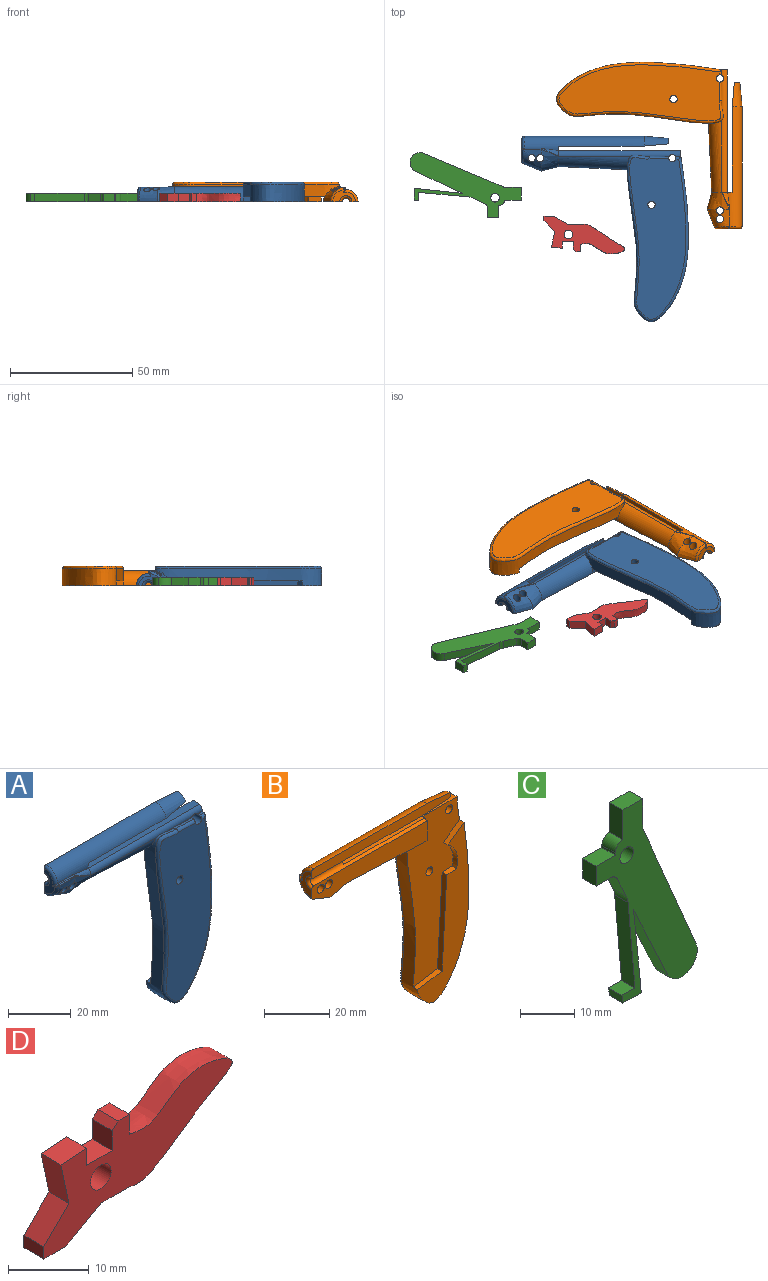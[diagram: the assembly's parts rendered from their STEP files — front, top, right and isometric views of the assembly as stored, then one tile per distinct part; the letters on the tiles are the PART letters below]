
ASSEMBLY  parts=4 mates=2
PART A: 55 faces, bbox 68.7x11.1x76.8 mm
  f0: plane 6.97x5.07mm, normal (-0.59,0,0.81), area 17.2mm2, adj f1,f22,f32,f54
  f1: extruded ~68.03x24.91mm, area 868.2mm2, adj f0,f6,f7,f8,f9,f10,f11,f22
  f2: cylinder r=1.5mm len=6mm, axis (0,1,0), area 56.5mm2, adj f22,f25
  f3: cylinder r=1.5mm len=6mm, axis (0,-1,0), area 49.7mm2, adj f5,f7,f8,f22,f23,f24,f25,f26
  f4: plane 7.88x2mm, normal (1,0,0), area 15.4mm2, adj f12,f13,f22,f30,f52
  f5: extruded ~7.96x0.14mm, area 0.5mm2, adj f3,f8,f23
  f6: extruded ~2.28x0.17mm, area 0.3mm2, adj f1,f8,f9
  f7: extruded ~2.24x0.24mm, area 0.4mm2, adj f1,f3,f8,f11,f24
  f8: cylinder r=2mm len=50mm, axis (1,0,0), area 131.6mm2, adj f1,f3,f5,f6,f7,f9,f10,f11
  f9: bspline ~35x2.96mm, area 0mm2, adj f1,f6,f8
  f10: bspline ~35x9.07mm, area 238.8mm2, adj f1,f8,f36,f49,f52
  f11: plane 4.12x2.43mm, normal (1,0,0), area 9.4mm2, adj f1,f7,f8,f13,f22
  f12: cylinder r=1.5mm len=49mm, axis (-1,0,0), area 154.3mm2, adj f4,f13,f16,f17,f20,f43,f52,f53
  f13: plane 50x3.78mm, normal (0,0,1), area 175.8mm2, adj f4,f8,f11,f12,f16,f22
  f14: cylinder r=5mm len=49mm, axis (-1,0,0), area 353.1mm2, adj f16,f17,f18,f35,f38,f41,f42,f53
  f15: plane 9.32x4.92mm, normal (-1,0,0), area 22.6mm2, adj f39,f40,f41,f43,f52,f53
  f16: plane 3.88x2mm, normal (1,0,0), area 7.2mm2, adj f12,f13,f14,f17
  f17: plane 35x3.78mm, normal (0,0,-1), area 132.3mm2, adj f12,f14,f16,f19
  f18: cone r=5mm half-angle=5deg, axis (-1,0,0), area 56.7mm2, adj f14,f19,f21,f53
  f19: plane 10.15x3.93mm, normal (0.09,0,-1), area 30.3mm2, adj f17,f18,f20,f21
  f20: cone r=1.5mm half-angle=5deg, axis (1,0,0), area 14.5mm2, adj f12,f19,f21,f53
  f21: plane 3.67x2.25mm, normal (1,0,0), area 5.4mm2, adj f18,f19,f20,f53
  f22: plane 62.43x23.55mm, normal (0,1,0), area 825.1mm2, adj f0,f1,f2,f3,f4,f11,f13,f29
  f23: plane 7.88x0.92mm, normal (0.02,0,1), area 7.2mm2, adj f1,f3,f5,f26
  f24: plane 2.14x0.93mm, normal (0.02,0,1), area 2mm2, adj f1,f3,f7,f28
  f25: plane 66.12x23.01mm, normal (0,-1,0), area 1183.2mm2, adj f2,f3,f26,f27,f28
  f26: cylinder r=1mm len=7.9mm, axis (1,0,-0.02), area 12.2mm2, adj f3,f23,f25,f27
  f27: bspline ~68.87x25.01mm, area 235.8mm2, adj f1,f25,f26,f28
  f28: cylinder r=1mm len=2.15mm, axis (1,0,-0.02), area 2.6mm2, adj f3,f24,f25,f27
  f29: plane 3.9x2mm, normal (-0.05,0,-1), area 7.8mm2, adj f1,f22,f30,f52
  f30: plane 3x2mm, normal (0,0,-1), area 6mm2, adj f4,f22,f29,f52
  f31: plane 4.22x2mm, normal (-0.01,0,1), area 8.4mm2, adj f22,f32,f34,f54
  f32: cylinder r=9.32mm len=10.8mm, axis (0,-1,0), area 24.5mm2, adj f0,f22,f31,f54
  f33: plane 10.54x2mm, normal (-0.16,0,0.99), area 21.4mm2, adj f1,f22,f34,f54
  f34: plane 35.08x2.01mm, normal (-1,0,0.06), area 70.3mm2, adj f22,f31,f33,f54
  f35: bspline ~6.93x3.14mm, area 10.4mm2, adj f8,f14,f42,f49
  f36: bspline ~9.22x7.64mm, area 67mm2, adj f10,f37,f48,f49,f50,f52
  f37: bspline ~9.22x8mm, area 64.2mm2, adj f36,f40,f45,f46,f47,f50,f51,f52
  f38: plane 6.93x0.7mm, normal (0,0,1), area 4.8mm2, adj f14,f39,f42,f46
  f39: cylinder r=1mm len=1.82mm, axis (0,1,0), area 1.3mm2, adj f15,f38,f41,f44,f45
  f40: bspline ~6.69x6.19mm, area 11.5mm2, adj f15,f37,f44,f52
  f41: torus R=4mm, axis (1,0,0), area 12.3mm2, adj f14,f15,f39,f53
  f42: bspline ~0.95x0.37mm, area 0.2mm2, adj f14,f35,f38,f47,f48
  f43: torus R=2.5mm, axis (1,0,0), area 9.2mm2, adj f12,f15,f52,f53
  f44: bspline ~1.18x1.1mm, area 0.4mm2, adj f39,f40,f45
  f45: bspline ~0.38x0.33mm, area 0mm2, adj f37,f39,f44,f46
  f46: bspline ~9.22x0.32mm, area 3.3mm2, adj f37,f38,f45,f47
  f47: bspline ~0.69x0.38mm, area 0.1mm2, adj f37,f42,f46,f48
  f48: bspline ~0.45x0.39mm, area 0mm2, adj f36,f42,f47,f49
  f49: bspline ~9.42x4.26mm, area 1.3mm2, adj f8,f10,f35,f36,f48
  f50: cylinder r=1.5mm len=5.76mm, axis (0,-1,0), area 49.5mm2, adj f36,f37,f52
  f51: cylinder r=1.5mm len=5.66mm, axis (0,-1,0), area 46.8mm2, adj f37,f52
  f52: plane 50.02x7.74mm, normal (0,1,0), area 316.7mm2, adj f4,f10,f12,f15,f29,f30,f36,f37
  f53: plane 60x3.5mm, normal (0,1,0), area 200.8mm2, adj f12,f14,f15,f18,f20,f21,f41,f43
  f54: plane 61.62x23.07mm, normal (0,1,0), area 509.6mm2, adj f0,f1,f31,f32,f33,f34
PART B: 55 faces, bbox 68.7x11.1x76.8 mm
  f0: plane 6.97x5.07mm, normal (-0.59,0,0.81), area 17.2mm2, adj f1,f13,f34,f54
  f1: extruded ~68.03x24.91mm, area 868.2mm2, adj f0,f3,f10,f14,f24,f25,f28,f29
  f2: plane 7.88x2mm, normal (1,0,0), area 15.4mm2, adj f4,f11,f27,f34,f52
  f3: bspline ~35x9.07mm, area 238.8mm2, adj f1,f16,f32,f51,f52
  f4: cylinder r=1.5mm len=49mm, axis (-1,0,0), area 154.3mm2, adj f2,f8,f20,f27,f30,f31,f52,f53
  f5: cylinder r=5mm len=49mm, axis (-1,0,0), area 353.1mm2, adj f7,f19,f30,f31,f42,f43,f45,f53
  f6: plane 9.32x4.92mm, normal (-1,0,0), area 22.6mm2, adj f18,f19,f20,f44,f52,f53
  f7: cone r=5mm half-angle=5deg, axis (-1,0,0), area 56.7mm2, adj f5,f9,f33,f53
  f8: cone r=1.5mm half-angle=5deg, axis (1,0,0), area 14.5mm2, adj f4,f9,f33,f53
  f9: plane 3.67x2.25mm, normal (1,0,0), area 5.4mm2, adj f7,f8,f33,f53
  f10: plane 3.9x2mm, normal (-0.05,0,-1), area 7.8mm2, adj f1,f11,f34,f52
  f11: plane 3x2mm, normal (0,0,-1), area 6mm2, adj f2,f10,f34,f52
  f12: plane 4.22x2mm, normal (-0.01,0,1), area 8.4mm2, adj f13,f15,f34,f54
  f13: cylinder r=9.32mm len=10.8mm, axis (0,-1,0), area 24.5mm2, adj f0,f12,f34,f54
  f14: plane 10.54x2mm, normal (-0.16,0,0.99), area 21.4mm2, adj f1,f15,f34,f54
  f15: plane 35.08x2.01mm, normal (-1,0,0.06), area 70.3mm2, adj f12,f14,f34,f54
  f16: bspline ~9.22x7.64mm, area 67mm2, adj f3,f17,f21,f50,f51,f52
  f17: bspline ~8.98x7.37mm, area 64.2mm2, adj f16,f18,f21,f22,f47,f48,f49,f52
  f18: bspline ~6.73x6.23mm, area 11.5mm2, adj f6,f17,f46,f52
  f19: torus R=4mm, axis (1,0,0), area 12.3mm2, adj f5,f6,f44,f53
  f20: torus R=2.5mm, axis (1,0,0), area 9.2mm2, adj f4,f6,f52,f53
  f21: cylinder r=1.5mm len=5.76mm, axis (0,-1,0), area 49.5mm2, adj f16,f17,f52
  f22: cylinder r=1.5mm len=5.66mm, axis (0,-1,0), area 46.8mm2, adj f17,f52
  f23: cylinder r=1.5mm len=6mm, axis (0,-1,0), area 49.7mm2, adj f25,f26,f32,f34,f35,f36,f37,f39
  f24: bspline ~35x2.96mm, area 0mm2, adj f1,f28,f32
  f25: extruded ~2.24x0.24mm, area 0.4mm2, adj f1,f23,f29,f32,f36
  f26: extruded ~7.96x0.14mm, area 0.5mm2, adj f23,f32,f35
  f27: plane 50x3.78mm, normal (0,0,1), area 175.8mm2, adj f2,f4,f29,f30,f32,f34
  f28: extruded ~2.28x0.17mm, area 0.3mm2, adj f1,f24,f32
  f29: plane 4.12x2.43mm, normal (1,0,0), area 9.4mm2, adj f1,f25,f27,f32,f34
  f30: plane 3.88x2mm, normal (1,0,0), area 7.2mm2, adj f4,f5,f27,f31
  f31: plane 35x3.78mm, normal (0,0,-1), area 132.3mm2, adj f4,f5,f30,f33
  f32: cylinder r=2mm len=50mm, axis (-1,0,0), area 131.6mm2, adj f1,f3,f23,f24,f25,f26,f27,f28
  f33: plane 10.15x3.93mm, normal (0.09,0,-1), area 30.3mm2, adj f7,f8,f9,f31
  f34: plane 62.43x23.55mm, normal (0,-1,0), area 825.1mm2, adj f0,f1,f2,f10,f11,f12,f13,f14
  f35: plane 7.88x0.92mm, normal (0.02,0,1), area 7.2mm2, adj f1,f23,f26,f39
  f36: plane 2.14x0.93mm, normal (0.02,0,1), area 2mm2, adj f1,f23,f25,f41
  f37: plane 66.12x23.01mm, normal (0,1,0), area 1183.1mm2, adj f23,f38,f39,f40,f41
  f38: cylinder r=1.5mm len=6mm, axis (0,1,0), area 56.5mm2, adj f34,f37
  f39: cylinder r=1mm len=7.9mm, axis (-1,0,0.02), area 12.2mm2, adj f23,f35,f37,f40
  f40: bspline ~68.88x25.01mm, area 235.9mm2, adj f1,f37,f39,f41
  f41: cylinder r=1mm len=2.15mm, axis (-1,0,0.02), area 2.6mm2, adj f23,f36,f37,f40
  f42: bspline ~6.93x3.14mm, area 10.4mm2, adj f5,f32,f45,f51
  f43: plane 6.93x0.7mm, normal (0,0,1), area 4.8mm2, adj f5,f44,f45,f48
  f44: cylinder r=1mm len=1.82mm, axis (0,1,0), area 1.3mm2, adj f6,f19,f43,f46,f47
  f45: bspline ~0.95x0.37mm, area 0.2mm2, adj f5,f42,f43,f49,f50
  f46: bspline ~1.18x1.1mm, area 0.4mm2, adj f18,f44,f47
  f47: bspline ~0.38x0.33mm, area 0mm2, adj f17,f44,f46,f48
  f48: bspline ~9.22x0.32mm, area 3.3mm2, adj f17,f43,f47,f49
  f49: bspline ~0.68x0.38mm, area 0.1mm2, adj f17,f45,f48,f50
  f50: bspline ~0.45x0.38mm, area 0mm2, adj f16,f45,f49,f51
  f51: bspline ~9.67x4.37mm, area 1.3mm2, adj f3,f16,f32,f42,f50
  f52: plane 50.02x7.74mm, normal (0,-1,0), area 316.7mm2, adj f2,f3,f4,f6,f10,f11,f16,f17
  f53: plane 60x3.5mm, normal (0,-1,0), area 200.8mm2, adj f4,f5,f6,f7,f8,f9,f19,f20
  f54: plane 61.62x23.07mm, normal (0,-1,0), area 509.6mm2, adj f0,f1,f12,f13,f14,f15
PART C: 26 faces, bbox 26.5x3.5x45.5 mm
  f0: plane 19.21x8.96mm, normal (-0.91,0,-0.42), area 74.2mm2, adj f9,f10,f16,f20
  f1: plane 3.5x0.5mm, normal (-1,0,0), area 1.8mm2, adj f9,f10,f11,f14
  f2: plane 5.1x3.5mm, normal (-0.91,0,-0.42), area 19.7mm2, adj f9,f10,f15,f25
  f3: plane 3.5x0.13mm, normal (0.39,0,-0.92), area 0.5mm2, adj f9,f10,f16,f17
  f4: plane 32.43x13.67mm, normal (0.92,0,0.39), area 123.2mm2, adj f9,f10,f17,f18
  f5: plane 5.89x3.5mm, normal (1,0,0), area 20.6mm2, adj f6,f9,f10,f18
  f6: plane 5.2x3.5mm, normal (0,0,1), area 18.2mm2, adj f5,f7,f9,f10
  f7: plane 6.7x3.5mm, normal (-1,0,0), area 23.4mm2, adj f6,f9,f10,f14
  f8: cylinder r=1.75mm len=3.5mm, axis (0,1,0), area 38.5mm2, adj f9,f10
  f9: plane 45.48x26.5mm, normal (0,-1,0), area 433.5mm2, adj f0,f1,f2,f3,f4,f5,f6,f7
  f10: plane 45.48x26.5mm, normal (0,1,0), area 433.5mm2, adj f0,f1,f2,f3,f4,f5,f6,f7
  f11: plane 5x3.5mm, normal (0,0,1), area 17.5mm2, adj f1,f9,f10,f13
  f12: plane 3.73x3.5mm, normal (0,0,-1), area 13mm2, adj f9,f10,f13,f15
  f13: plane 4.5x3.5mm, normal (-1,0,0), area 15.8mm2, adj f9,f10,f11,f12
  f14: cylinder r=2mm len=3.5mm, axis (0,1,0), area 11mm2, adj f1,f7,f9,f10
  f15: cylinder r=2mm len=3.5mm, axis (0,-1,0), area 7.9mm2, adj f2,f9,f10,f12
  f16: cylinder r=4mm len=5.18mm, axis (0,1,0), area 21.5mm2, adj f0,f3,f9,f10
  f17: cylinder r=4mm len=5.24mm, axis (0,1,0), area 22mm2, adj f3,f4,f9,f10
  f18: cylinder r=4mm len=3.5mm, axis (0,-1,0), area 5.6mm2, adj f4,f5,f9,f10
  f19: plane 20.31x3.5mm, normal (-1,0,-0.09), area 71.4mm2, adj f9,f10,f24,f25
  f20: plane 18.05x3.5mm, normal (0.99,0,0.1), area 63.5mm2, adj f0,f9,f10,f21
  f21: plane 3.5x1.8mm, normal (1,0,0.07), area 6.3mm2, adj f9,f10,f20,f22
  f22: plane 4.79x3.5mm, normal (-0.02,0,-1), area 16.8mm2, adj f9,f10,f21,f23
  f23: plane 3.5x1.8mm, normal (-0.99,0,-0.13), area 6.4mm2, adj f9,f10,f22,f24
  f24: plane 3.5x3.41mm, normal (0,0,1), area 11.9mm2, adj f9,f10,f19,f23
  f25: cylinder r=5mm len=3.5mm, axis (0,1,0), area 6.1mm2, adj f2,f9,f10,f19
PART D: 17 faces, bbox 33.3x3.5x15.8 mm
  f0: plane 5x3.5mm, normal (0,0,-1), area 17.5mm2, adj f7,f8,f13,f16
  f1: plane 4.5x3.5mm, normal (0,0,1), area 15.8mm2, adj f4,f7,f8,f9
  f2: plane 6.52x3.5mm, normal (-0.98,0,-0.21), area 23.3mm2, adj f5,f7,f8,f12
  f3: plane 3.5x3mm, normal (1,0,0), area 10.5mm2, adj f7,f8,f10,f16
  f4: plane 3.5x2.6mm, normal (1,0,0), area 9.1mm2, adj f1,f5,f7,f8
  f5: plane 4.49x3.5mm, normal (-0.07,0,1), area 15.8mm2, adj f2,f4,f7,f8
  f6: cylinder r=1.8mm len=3.6mm, axis (0,1,0), area 39.6mm2, adj f7,f8
  f7: plane 33.34x15.77mm, normal (0,-1,0), area 226.8mm2, adj f0,f1,f2,f3,f4,f5,f6,f9
  f8: plane 33.04x15.45mm, normal (0,1,0), area 225.1mm2, adj f0,f1,f2,f3,f4,f5,f6,f9
  f9: plane 3.5x3mm, normal (-1,0,0), area 10.5mm2, adj f1,f7,f8,f11
  f10: plane 3.5x2mm, normal (0,0,1), area 7mm2, adj f3,f7,f8,f11
  f11: plane 3.5x1mm, normal (-0.71,0,0.71), area 4.9mm2, adj f7,f8,f9,f10
  f12: plane 4.41x4.41mm, normal (-0.71,0,0.71), area 21.8mm2, adj f2,f7,f8,f15
  f13: plane 6.05x3.5mm, normal (0.5,0,-0.87), area 24.4mm2, adj f0,f7,f8,f14
  f14: plane 3.95x3.5mm, normal (0,0,-1), area 13.8mm2, adj f7,f8,f13,f15
  f15: plane 3.5x1.85mm, normal (-1,0,0), area 6.5mm2, adj f7,f8,f12,f14
  f16: extruded ~18.03x12.17mm, area 142.9mm2, adj f0,f3,f7,f8
PLACE A rot(axis=(-1,0,0),90deg) t=(-19.04,35.16,0)mm
PLACE B rot(axis=(0.58,0.58,0.58),120deg) t=(65.95,2.28,0)mm
PLACE C rot(axis=(0.58,0.58,0.58),120deg) t=(-26,12,1.9)mm
PLACE D rot(axis=(1,0,0),90deg) t=(-61.5,-4,1.9)mm
MATE fastened A.f54 <-> D.f7  axis (0,0,-1) through (40,20,0)mm
MATE fastened B.f54 <-> D.f7  axis (0,0,-1) through (40,65,0)mm
